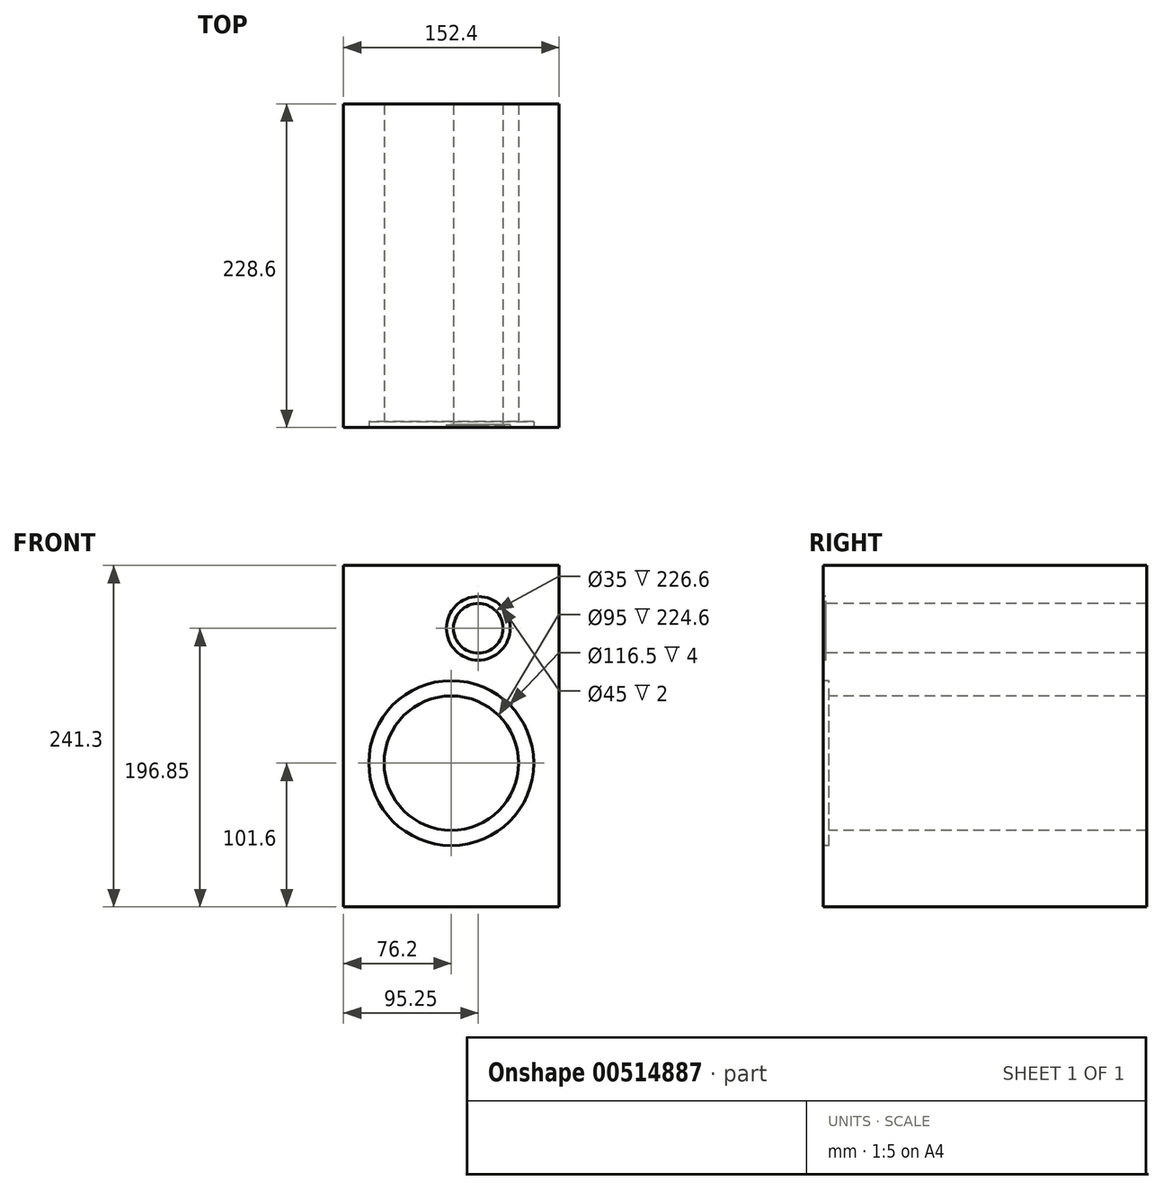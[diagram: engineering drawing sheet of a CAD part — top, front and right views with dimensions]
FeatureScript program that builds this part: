
annotation { "Feature Type Name" : "Feature", "Feature Type Description" : "" }
export const myFeature = defineFeature(function(context is Context, id is Id, definition is map)
    precondition{}
    {
        {
            var Q0;
            Q0=qCreatedBy(makeId("Top.planeOp"),FACE);
            var sketch = newSketch(context, id + "F0", { "sketchPlane" : qUnion([Q0])});
            skLineSegment(sketch, "E0.bottom", {"start": v(-76.2, 0) * mm, "end": v(76.2, 0) * mm});
            skLineSegment(sketch, "E0.top", {"start": v(-76.2, 228.6) * mm, "end": v(76.2, 228.6) * mm});
            skLineSegment(sketch, "E0.left", {"start": v(-76.2, 0) * mm, "end": v(-76.2, 228.6) * mm});
            skLineSegment(sketch, "E0.right", {"start": v(76.2, 0) * mm, "end": v(76.2, 228.6) * mm});
            skSolve(sketch);
        }
        {
            var Q0;
            Q0=makeQuery(id+"F0.imprint","IMPRINT",FACE,{"disambiguationData":[TD([[makeQuery(id+"F0.imprint","IMPRINT",EDGE,{"derivedFrom":sQuery(id+"F0.wireOp",EDGE,"E0.bottom")}),1.0]])]});
            extrude(context, id + "F1", {"entities" : qUnion([Q0]), "depth" : 241.3 * mm, "offsetDistance" : 25.4 * mm});
        }
        {
            var Q0;
            Q0=makeQuery(id+"F1.opExtrude","SWEPT_FACE",FACE,{"disambiguationData":[OSD([sQuery(id+"F0.wireOp",EDGE,"E0.bottom")])]});
            var sketch = newSketch(context, id + "F2", { "sketchPlane" : qUnion([Q0])});
            skCircle(sketch, "E1", {"center": v(0, 101.6) * mm, "radius": 47.5 * mm});
            skCircle(sketch, "E2", {"center": v(19.05, 196.85) * mm, "radius": 17.5 * mm});
            skSolve(sketch);
        }
        {
            var Q0;
            Q0 = qSketchRegion(id + "F2", true);
            extrude(context, id + "F3", {"entities" : qUnion([Q0]), "operationType" : NewBodyOperationType.REMOVE, "endBound" : BoundingType.UP_TO_NEXT, "oppositeDirection" : true, "depth" : 25.4 * mm, "offsetDistance" : 25.4 * mm});
        }
        {
            var Q0;
            Q0=makeQuery(id+"F1.opExtrude","SWEPT_FACE",FACE,{"disambiguationData":[OSD([sQuery(id+"F0.wireOp",EDGE,"E0.bottom")])]});
            var sketch = newSketch(context, id + "F4", { "sketchPlane" : qUnion([Q0])});
            skCircle(sketch, "E3", {"center": v(0, 101.6) * mm, "radius": 58.25 * mm});
            skSolve(sketch);
        }
        {
            var Q0;
            Q0 = qSketchRegion(id + "F4", true);
            extrude(context, id + "F5", {"entities" : qUnion([Q0]), "operationType" : NewBodyOperationType.REMOVE, "oppositeDirection" : true, "depth" : 4 * mm, "offsetDistance" : 25.4 * mm});
        }
        {
            var Q0;
            Q0=makeQuery(id+"F1.opExtrude","SWEPT_FACE",FACE,{"disambiguationData":[OSD([sQuery(id+"F0.wireOp",EDGE,"E0.bottom")])]});
            var sketch = newSketch(context, id + "F6", { "sketchPlane" : qUnion([Q0])});
            skCircle(sketch, "E4", {"center": v(19.05, 196.85) * mm, "radius": 22.5 * mm});
            skSolve(sketch);
        }
        {
            var Q0;
            Q0 = qSketchRegion(id + "F6", true);
            extrude(context, id + "F7", {"entities" : qUnion([Q0]), "operationType" : NewBodyOperationType.REMOVE, "oppositeDirection" : true, "depth" : 2 * mm, "offsetDistance" : 25.4 * mm});
        }
    });
